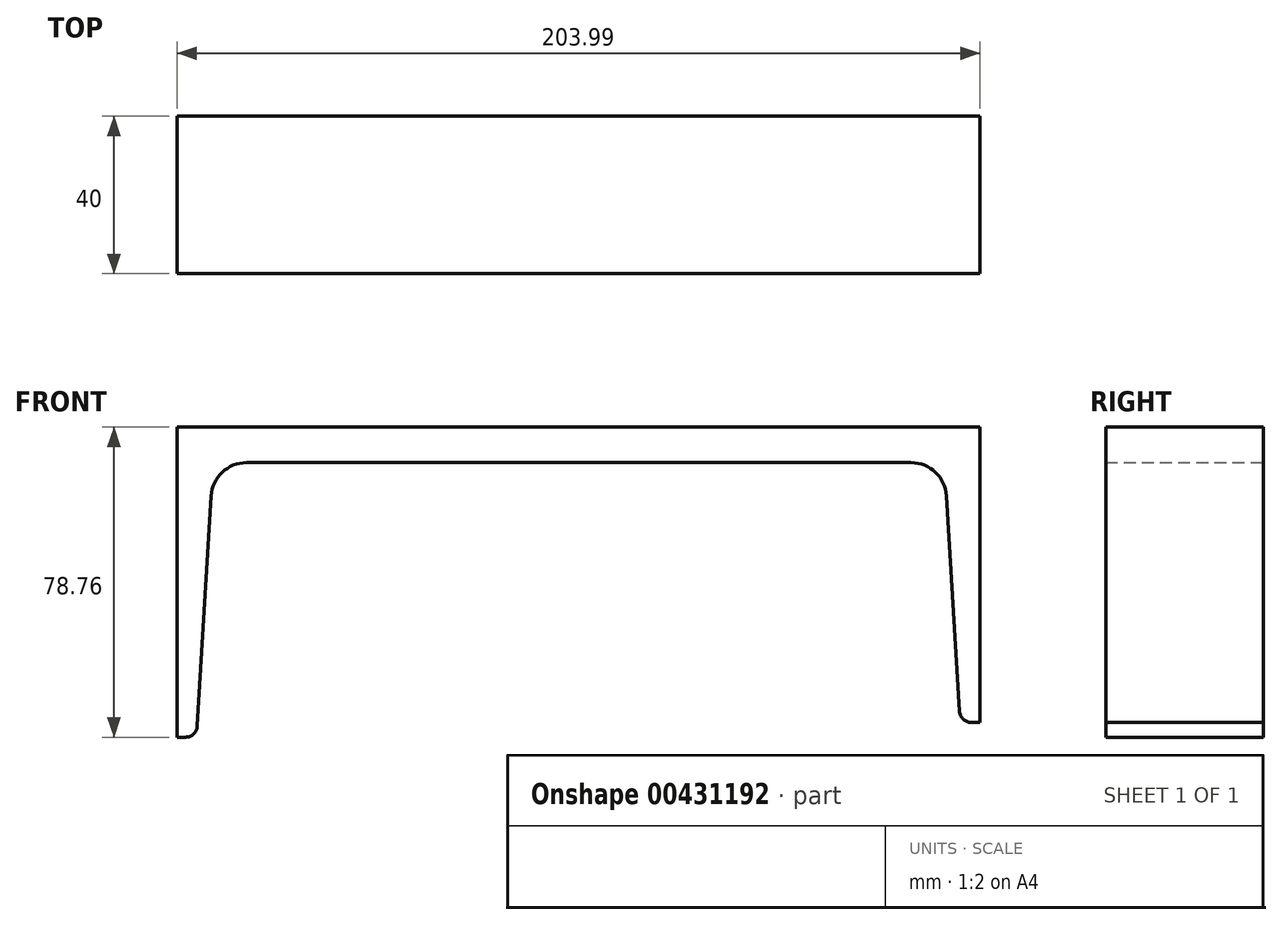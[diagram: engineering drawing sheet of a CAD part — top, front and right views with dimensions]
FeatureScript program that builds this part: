
annotation { "Feature Type Name" : "Feature", "Feature Type Description" : "" }
export const myFeature = defineFeature(function(context is Context, id is Id, definition is map)
    precondition{}
    {
        {
            var Q0;
            Q0=qCreatedBy(makeId("Front.planeOp"),FACE);
            var sketch = newSketch(context, id + "F0", { "sketchPlane" : qUnion([Q0])});
            skLineSegment(sketch, "E0", {"start": v(204, 3.76) * mm, "end": v(204, 78.76) * mm});
            skLineSegment(sketch, "E1", {"start": v(204, 78.76) * mm, "end": v(0, 78.76) * mm});
            skLineSegment(sketch, "E2", {"start": v(0, 78.76) * mm, "end": v(0, 0) * mm});
            skLineSegment(sketch, "E3.0", {"start": v(186.52, 69.76) * mm, "end": v(17.7, 69.76) * mm});
            skLineSegment(sketch, "E4", {"start": v(0, 0) * mm, "end": v(2.18, 0) * mm});
            skLineSegment(sketch, "E5", {"start": v(204, 3.76) * mm, "end": v(201.82, 3.76) * mm});
            skLineSegment(sketch, "E6", {"start": v(5.17, 2.82) * mm, "end": v(8.72, 61.3) * mm});
            skLineSegment(sketch, "E7", {"start": v(198.82, 6.58) * mm, "end": v(195.5, 61.3) * mm});
            skArc(sketch, "E8.filletArc", {"start": v(17.7, 69.76) * mm, "mid": v(11.53, 67.31) * mm, "end": v(8.72, 61.3) * mm});
            skArc(sketch, "E9.filletArc", {"start": v(195.5, 61.3) * mm, "mid": v(192.7, 67.31) * mm, "end": v(186.52, 69.76) * mm});
            skPoint(sketch, "E10.visualSharp", {"position": v(5, 0) * mm});
            skArc(sketch, "E10.filletArc", {"start": v(2.18, 0) * mm, "mid": v(4.23, 0.82) * mm, "end": v(5.17, 2.82) * mm});
            skArc(sketch, "E11.filletArc", {"start": v(198.82, 6.58) * mm, "mid": v(199.76, 4.57) * mm, "end": v(201.82, 3.76) * mm});
            skSolve(sketch);
        }
        {
            var Q0;
            Q0=makeQuery(id+"F0.imprint","IMPRINT",FACE,{"disambiguationData":[TD([[makeQuery(id+"F0.imprint","IMPRINT",EDGE,{"derivedFrom":sQuery(id+"F0.wireOp",EDGE,"E0")}),1.0]])]});
            extrude(context, id + "F1", {"entities" : qUnion([Q0]), "depth" : 40 * mm});
        }
    });
